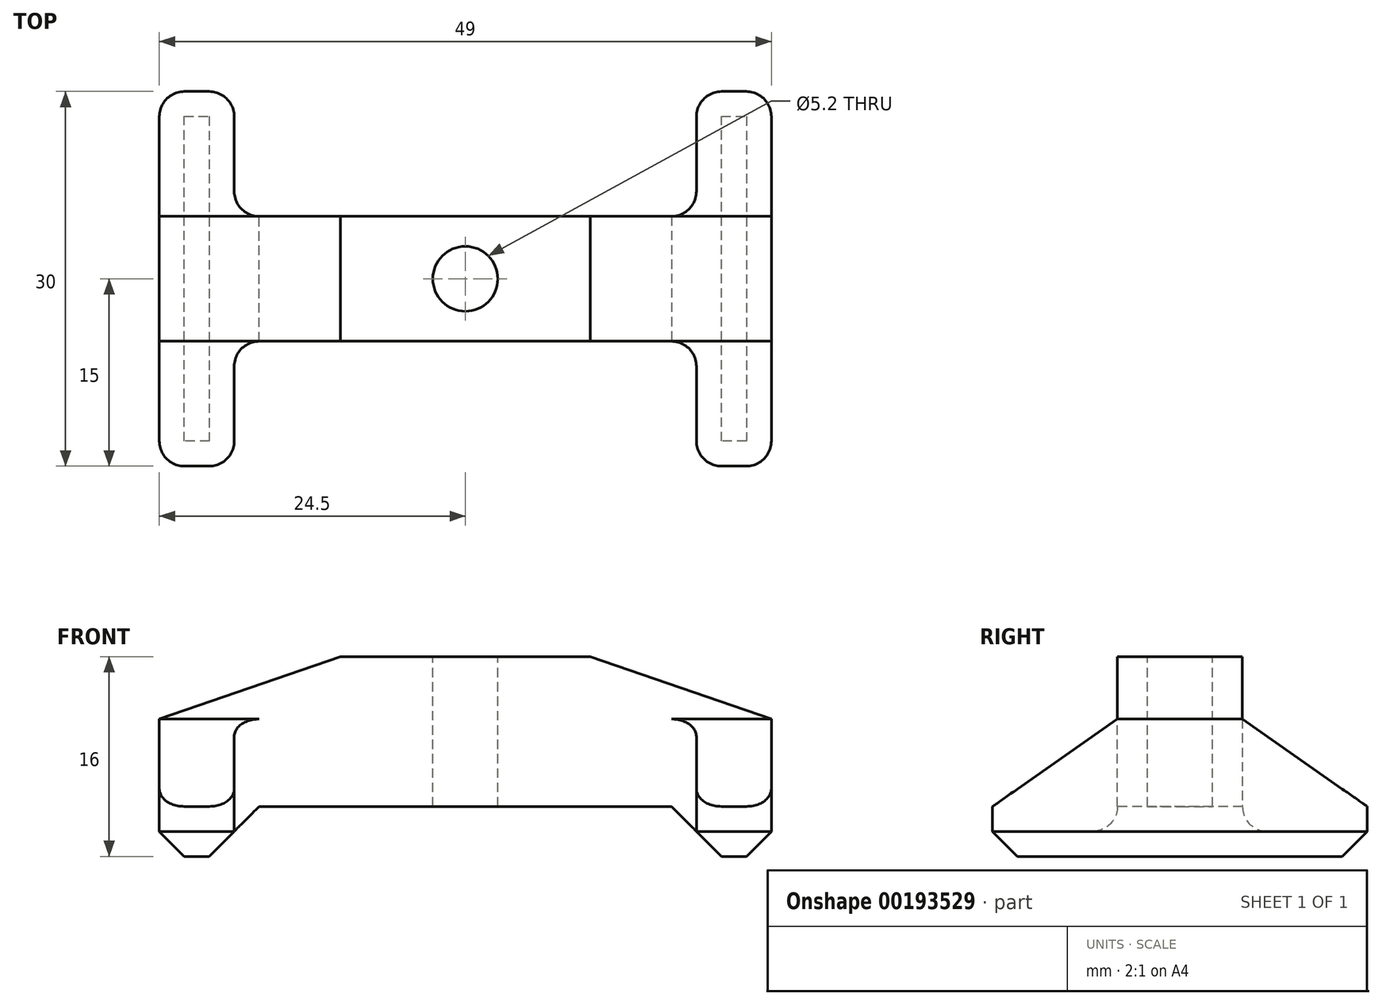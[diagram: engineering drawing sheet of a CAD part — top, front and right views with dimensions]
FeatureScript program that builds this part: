
annotation { "Feature Type Name" : "Feature", "Feature Type Description" : "" }
export const myFeature = defineFeature(function(context is Context, id is Id, definition is map)
    precondition{}
    {
        {
            var Q0;
            Q0=qCreatedBy(makeId("Front.planeOp"),FACE);
            var sketch = newSketch(context, id + "F0", { "sketchPlane" : qUnion([Q0])});
            skLineSegment(sketch, "E0", {"start": v(-24.5, 0) * mm, "end": v(24.5, 0) * mm});
            skLineSegment(sketch, "E1", {"start": v(24.5, 0) * mm, "end": v(24.5, 7) * mm});
            skLineSegment(sketch, "E2", {"start": v(24.5, 7) * mm, "end": v(10, 12) * mm});
            skLineSegment(sketch, "E3", {"start": v(10, 12) * mm, "end": v(-10, 12) * mm});
            skLineSegment(sketch, "E4", {"start": v(-10, 12) * mm, "end": v(-24.5, 7) * mm});
            skLineSegment(sketch, "E5", {"start": v(-24.5, 7) * mm, "end": v(-24.5, 0) * mm});
            skPoint(sketch, "E6", {"position": v(0, 12) * mm});
            skSolve(sketch);
        }
        {
            var Q0;
            Q0=makeQuery(id+"F0.imprint","IMPRINT",FACE,{"disambiguationData":[TD([[makeQuery(id+"F0.imprint","IMPRINT",EDGE,{"derivedFrom":sQuery(id+"F0.wireOp",EDGE,"E0")}),1.0]])]});
            extrude(context, id + "F1", {"entities" : qUnion([Q0]), "endBound" : BoundingType.SYMMETRIC, "depth" : 10 * mm});
        }
        {
            var Q0;
            Q0=makeQuery(id+"F1.opExtrude","SWEPT_FACE",FACE,{"disambiguationData":[OSD([sQuery(id+"F0.wireOp",EDGE,"E5")])]});
            var sketch = newSketch(context, id + "F2", { "sketchPlane" : qUnion([Q0])});
            skLineSegment(sketch, "E7", {"start": v(-15, -4) * mm, "end": v(15, -4) * mm});
            skLineSegment(sketch, "E8", {"start": v(15, -4) * mm, "end": v(15, 0) * mm});
            skLineSegment(sketch, "E9", {"start": v(15, 0) * mm, "end": v(5, 7) * mm});
            skLineSegment(sketch, "E10", {"start": v(5, 7) * mm, "end": v(-5, 7) * mm});
            skLineSegment(sketch, "E11", {"start": v(-5, 7) * mm, "end": v(-15, 0) * mm});
            skLineSegment(sketch, "E12", {"start": v(-15, 0) * mm, "end": v(-15, -4) * mm});
            skPoint(sketch, "E13", {"position": v(0, -4) * mm});
            skSolve(sketch);
        }
        {
            var Q0;
            Q0 = qSketchRegion(id + "F2", true);
            extrude(context, id + "F3", {"entities" : qUnion([Q0]), "oppositeDirection" : true, "depth" : 6 * mm});
        }
        {
            var Q0;
            Q0=makeQuery(id+"F3.opExtrude","SWEPT_BODY",BODY,{"disambiguationData":[OSD([sQuery(id+"F2.wireOp",EDGE,"E7"),sQuery(id+"F2.wireOp",EDGE,"E8"),sQuery(id+"F2.wireOp",EDGE,"E9"),sQuery(id+"F2.wireOp",EDGE,"E10"),sQuery(id+"F2.wireOp",EDGE,"E11"),sQuery(id+"F2.wireOp",EDGE,"E12")])]});
            var Q1;
            Q1=qCreatedBy(makeId("Right.planeOp"),FACE);
            mirror(context, id + "F4", {"operationType" : NewBodyOperationType.ADD, "entities" : qUnion([Q0]), "mirrorPlane" : qUnion([Q1])});
        }
        {
            var Q0;
            Q0=makeQuery(id+"F1.opExtrude","SWEPT_FACE",FACE,{"disambiguationData":[OSD([sQuery(id+"F0.wireOp",EDGE,"E3")])]});
            var sketch = newSketch(context, id + "F5", { "sketchPlane" : qUnion([Q0])});
            skCircle(sketch, "E14", {"center": v(0, 0) * mm, "radius": 2.6 * mm});
            skSolve(sketch);
        }
        {
            var Q0;
            Q0 = qSketchRegion(id + "F5", true);
            extrude(context, id + "F6", {"entities" : qUnion([Q0]), "operationType" : NewBodyOperationType.REMOVE, "endBound" : BoundingType.THROUGH_ALL, "oppositeDirection" : true, "depth" : 25 * mm});
        }
        {
            var Q0;
            Q0=makeQuery(id+"F4.opPattern","COPY",EDGE,{"derivedFrom":makeQuery(id+"F3.opExtrude","CAP_EDGE",EDGE,{"disambiguationData":[OSD([sQuery(id+"F2.wireOp",EDGE,"E8")])],"isStart":true}),"instanceName":"1"});
            var Q1;
            Q1=makeQuery(id+"F4.opPattern","COPY",EDGE,{"derivedFrom":makeQuery(id+"F3.opExtrude","CAP_EDGE",EDGE,{"disambiguationData":[OSD([sQuery(id+"F2.wireOp",EDGE,"E8")])],"isStart":false}),"instanceName":"1"});
            var Q2;
            Q2=makeQuery(id+"F3.opExtrude","CAP_EDGE",EDGE,{"disambiguationData":[OSD([sQuery(id+"F2.wireOp",EDGE,"E8")])],"isStart":false});
            var Q3;
            Q3=makeQuery(id+"F3.opExtrude","CAP_EDGE",EDGE,{"disambiguationData":[OSD([sQuery(id+"F2.wireOp",EDGE,"E8")])],"isStart":true});
            var Q4;
            Q4=makeQuery(id+"F4.opPattern","COPY",EDGE,{"derivedFrom":makeQuery(id+"F3.opExtrude","CAP_EDGE",EDGE,{"disambiguationData":[OSD([sQuery(id+"F2.wireOp",EDGE,"E12")])],"isStart":true}),"instanceName":"1"});
            var Q5;
            Q5=makeQuery(id+"F3.opExtrude","CAP_EDGE",EDGE,{"disambiguationData":[OSD([sQuery(id+"F2.wireOp",EDGE,"E12")])],"isStart":false});
            var Q6;
            Q6=makeQuery(id+"F3.opExtrude","CAP_EDGE",EDGE,{"disambiguationData":[OSD([sQuery(id+"F2.wireOp",EDGE,"E12")])],"isStart":true});
            var Q7;
            Q7=makeQuery(id+"F4.opPattern","COPY",EDGE,{"derivedFrom":makeQuery(id+"F3.opExtrude","CAP_EDGE",EDGE,{"disambiguationData":[OSD([sQuery(id+"F2.wireOp",EDGE,"E12")])],"isStart":false}),"instanceName":"1"});
            var Q8;
            Q8=makeQuery(id+"F4.boolean.opBoolean","INTERSECT",EDGE,{"derivedFrom":[makeQuery(id+"F1.opExtrude","CAP_FACE",FACE,{"disambiguationData":[OSD([sQuery(id+"F0.wireOp",EDGE,"E0"),sQuery(id+"F0.wireOp",EDGE,"E1"),sQuery(id+"F0.wireOp",EDGE,"E2"),sQuery(id+"F0.wireOp",EDGE,"E3"),sQuery(id+"F0.wireOp",EDGE,"E4"),sQuery(id+"F0.wireOp",EDGE,"E5")])],"isStart":false}),makeQuery(id+"F3.opExtrude","CAP_FACE",FACE,{"disambiguationData":[OSD([sQuery(id+"F2.wireOp",EDGE,"E7"),sQuery(id+"F2.wireOp",EDGE,"E8"),sQuery(id+"F2.wireOp",EDGE,"E9"),sQuery(id+"F2.wireOp",EDGE,"E10"),sQuery(id+"F2.wireOp",EDGE,"E11"),sQuery(id+"F2.wireOp",EDGE,"E12")])],"isStart":false})]});
            var Q9;
            Q9=makeQuery(id+"F4.boolean.opBoolean","INTERSECT",EDGE,{"derivedFrom":[makeQuery(id+"F1.opExtrude","CAP_FACE",FACE,{"disambiguationData":[OSD([sQuery(id+"F0.wireOp",EDGE,"E0"),sQuery(id+"F0.wireOp",EDGE,"E1"),sQuery(id+"F0.wireOp",EDGE,"E2"),sQuery(id+"F0.wireOp",EDGE,"E3"),sQuery(id+"F0.wireOp",EDGE,"E4"),sQuery(id+"F0.wireOp",EDGE,"E5")])],"isStart":false}),makeQuery(id+"F4.opPattern","COPY",FACE,{"derivedFrom":makeQuery(id+"F3.opExtrude","CAP_FACE",FACE,{"disambiguationData":[OSD([sQuery(id+"F2.wireOp",EDGE,"E7"),sQuery(id+"F2.wireOp",EDGE,"E8"),sQuery(id+"F2.wireOp",EDGE,"E9"),sQuery(id+"F2.wireOp",EDGE,"E10"),sQuery(id+"F2.wireOp",EDGE,"E11"),sQuery(id+"F2.wireOp",EDGE,"E12")])],"isStart":false}),"instanceName":"1"})]});
            var Q10;
            Q10=makeQuery(id+"F4.boolean.opBoolean","INTERSECT",EDGE,{"derivedFrom":[makeQuery(id+"F1.opExtrude","CAP_FACE",FACE,{"disambiguationData":[OSD([sQuery(id+"F0.wireOp",EDGE,"E0"),sQuery(id+"F0.wireOp",EDGE,"E1"),sQuery(id+"F0.wireOp",EDGE,"E2"),sQuery(id+"F0.wireOp",EDGE,"E3"),sQuery(id+"F0.wireOp",EDGE,"E4"),sQuery(id+"F0.wireOp",EDGE,"E5")])],"isStart":true}),makeQuery(id+"F4.opPattern","COPY",FACE,{"derivedFrom":makeQuery(id+"F3.opExtrude","CAP_FACE",FACE,{"disambiguationData":[OSD([sQuery(id+"F2.wireOp",EDGE,"E7"),sQuery(id+"F2.wireOp",EDGE,"E8"),sQuery(id+"F2.wireOp",EDGE,"E9"),sQuery(id+"F2.wireOp",EDGE,"E10"),sQuery(id+"F2.wireOp",EDGE,"E11"),sQuery(id+"F2.wireOp",EDGE,"E12")])],"isStart":false}),"instanceName":"1"})]});
            var Q11;
            Q11=makeQuery(id+"F4.boolean.opBoolean","INTERSECT",EDGE,{"derivedFrom":[makeQuery(id+"F1.opExtrude","CAP_FACE",FACE,{"disambiguationData":[OSD([sQuery(id+"F0.wireOp",EDGE,"E0"),sQuery(id+"F0.wireOp",EDGE,"E1"),sQuery(id+"F0.wireOp",EDGE,"E2"),sQuery(id+"F0.wireOp",EDGE,"E3"),sQuery(id+"F0.wireOp",EDGE,"E4"),sQuery(id+"F0.wireOp",EDGE,"E5")])],"isStart":true}),makeQuery(id+"F3.opExtrude","CAP_FACE",FACE,{"disambiguationData":[OSD([sQuery(id+"F2.wireOp",EDGE,"E7"),sQuery(id+"F2.wireOp",EDGE,"E8"),sQuery(id+"F2.wireOp",EDGE,"E9"),sQuery(id+"F2.wireOp",EDGE,"E10"),sQuery(id+"F2.wireOp",EDGE,"E11"),sQuery(id+"F2.wireOp",EDGE,"E12")])],"isStart":false})]});
            fillet(context, id + "F7", {"entities" : qUnion([Q0, Q1, Q2, Q3, Q4, Q5, Q6, Q7, Q8, Q9, Q10, Q11]), "radius" : 2 * mm, "tangentPropagation" : true, "allowEdgeOverflow" : false});
        }
        {
            var Q0;
            Q0=makeQuery(id+"F4.opPattern","COPY",EDGE,{"derivedFrom":makeQuery(id+"F3.opExtrude","CAP_EDGE",EDGE,{"disambiguationData":[OSD([sQuery(id+"F2.wireOp",EDGE,"E7")])],"isStart":true}),"instanceName":"1"});
            var Q1;
            Q1=makeQuery(id+"F3.opExtrude","CAP_EDGE",EDGE,{"disambiguationData":[OSD([sQuery(id+"F2.wireOp",EDGE,"E7")])],"isStart":false});
            var Q2;
            Q2=makeQuery(id+"F4.boolean.opBoolean","INTERSECT",EDGE,{"derivedFrom":[makeQuery(id+"F1.opExtrude","SWEPT_FACE",FACE,{"disambiguationData":[OSD([sQuery(id+"F0.wireOp",EDGE,"E0")])]}),makeQuery(id+"F3.opExtrude","CAP_FACE",FACE,{"disambiguationData":[OSD([sQuery(id+"F2.wireOp",EDGE,"E7"),sQuery(id+"F2.wireOp",EDGE,"E8"),sQuery(id+"F2.wireOp",EDGE,"E9"),sQuery(id+"F2.wireOp",EDGE,"E10"),sQuery(id+"F2.wireOp",EDGE,"E11"),sQuery(id+"F2.wireOp",EDGE,"E12")])],"isStart":false})]});
            var Q3;
            Q3=makeQuery(id+"F4.boolean.opBoolean","INTERSECT",EDGE,{"derivedFrom":[makeQuery(id+"F1.opExtrude","SWEPT_FACE",FACE,{"disambiguationData":[OSD([sQuery(id+"F0.wireOp",EDGE,"E0")])]}),makeQuery(id+"F4.opPattern","COPY",FACE,{"derivedFrom":makeQuery(id+"F3.opExtrude","CAP_FACE",FACE,{"disambiguationData":[OSD([sQuery(id+"F2.wireOp",EDGE,"E7"),sQuery(id+"F2.wireOp",EDGE,"E8"),sQuery(id+"F2.wireOp",EDGE,"E9"),sQuery(id+"F2.wireOp",EDGE,"E10"),sQuery(id+"F2.wireOp",EDGE,"E11"),sQuery(id+"F2.wireOp",EDGE,"E12")])],"isStart":false}),"instanceName":"1"})]});
            chamfer(context, id + "F8", {"entities" : qUnion([Q0, Q1, Q2, Q3]), "width" : 2 * mm, "tangentPropagation" : true});
        }
    });
